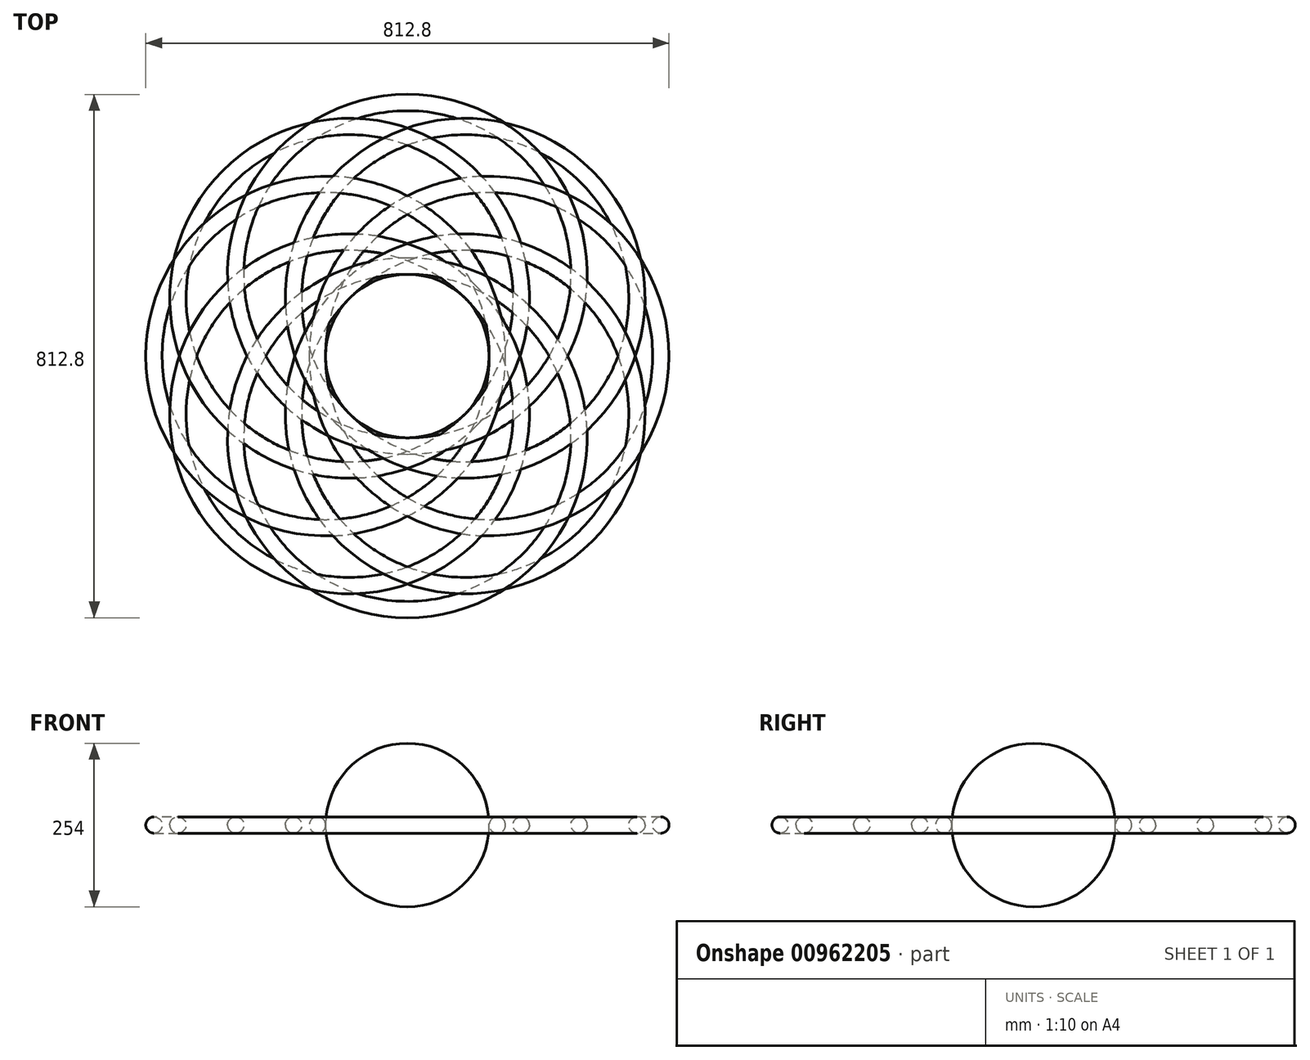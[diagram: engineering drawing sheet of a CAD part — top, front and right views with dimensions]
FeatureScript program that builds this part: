
annotation { "Feature Type Name" : "Feature", "Feature Type Description" : "" }
export const myFeature = defineFeature(function(context is Context, id is Id, definition is map)
    precondition{}
    {
        {
            var Q0;
            Q0=qCreatedBy(makeId("Top.planeOp"),FACE);
            var sketch = newSketch(context, id + "F0", { "sketchPlane" : qUnion([Q0])});
            skArc(sketch, "E0", {"start": v(0, -127) * mm, "mid": v(127, 0) * mm, "end": v(0, 127) * mm});
            skLineSegment(sketch, "E1", {"start": v(0, 127) * mm, "end": v(0, -127) * mm});
            skSolve(sketch);
        }
        {
            var Q0;
            Q0 = qSketchRegion(id + "F0", true);
            var Q1;
            Q1=sQuery(id+"F0.wireOp",EDGE,"E1");
            revolve(context, id + "F1", {"surfaceOperationType" : NewSurfaceOperationType.NEW, "entities" : qUnion([Q0]), "axis" : qUnion([Q1]), "revolveType" : RevolveType.FULL});
        }
        {
            var Q0;
            Q0=qCreatedBy(makeId("Top.planeOp"),FACE);
            var sketch = newSketch(context, id + "F2", { "sketchPlane" : qUnion([Q0])});
            skCircle(sketch, "E2", {"center": v(-127, 0) * mm, "radius": 254 * mm});
            skArc(sketch, "E3.0", {"start": v(0, -127) * mm, "mid": v(127, 0) * mm, "end": v(0, 127) * mm});
            skCircle(sketch, "E4.0", {"center": v(-127, 0) * mm, "radius": 266.7 * mm});
            skSolve(sketch);
        }
        {
            var Q0;
            Q0=qCreatedBy(makeId("Top.planeOp"),FACE);
            var sketch = newSketch(context, id + "F3", { "sketchPlane" : qUnion([Q0])});
            skCircle(sketch, "E5.0", {"center": v(-127, 0) * mm, "radius": 266.7 * mm});
            skSolve(sketch);
        }
        {
            var Q0;
            Q0=qCreatedBy(makeId("Front.planeOp"),FACE);
            var sketch = newSketch(context, id + "F4", { "sketchPlane" : qUnion([Q0])});
            skCircle(sketch, "E6", {"center": v(139.7, 0) * mm, "radius": 12.7 * mm});
            skLineSegment(sketch, "E7.0", {"start": v(-393.7, 0) * mm, "end": v(139.7, 0) * mm});
            skLineSegment(sketch, "E8.0", {"start": v(-381, 0) * mm, "end": v(127, 0) * mm});
            skSolve(sketch);
        }
        {
            var Q0;
            Q0=makeQuery(id+"F4.imprint","IMPRINT",FACE,{"disambiguationData":[TD([[makeQuery(id+"F4.imprint","IMPRINT",EDGE,{"derivedFrom":sQuery(id+"F4.wireOp",EDGE,"E6")}),1.0]])]});
            var Q1;
            Q1=sQuery(id+"F3.wireOp",EDGE,"E5.0");
            sweep(context, id + "F5", {"profiles" : qUnion([Q0]), "path" : qUnion([Q1])});
        }
        {
            var Q0;
            Q0=qCreatedBy(makeId("Right.planeOp"),FACE);
            var sketch = newSketch(context, id + "F6", { "sketchPlane" : qUnion([Q0])});
            skLineSegment(sketch, "E9", {"start": v(0, -32) * mm, "end": v(0, 125.32) * mm});
            skSolve(sketch);
        }
        {
            var Q0;
            Q0=makeQuery(id+"F5.opSweep","SWEPT_BODY",BODY,{"disambiguationData":[OSD([sQuery(id+"F3.wireOp",EDGE,"E5.0"),sQuery(id+"F4.wireOp",EDGE,"E6")])]});
            var Q1;
            Q1=sQuery(id+"F6.wireOp",EDGE,"E9");
            circularPattern(context, id + "F7", {"entities" : qUnion([Q0]), "axis" : qUnion([Q1]), "angle" : 360 * degree, "instanceCount" : 8, "equalSpace" : true});
        }
    });
